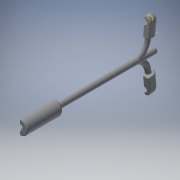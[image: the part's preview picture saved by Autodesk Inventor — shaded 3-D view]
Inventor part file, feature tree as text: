
AUTODESK INVENTOR PART (.ipt)
format: ipt  version: 2018 (Build 220112000, 112)  size: 584,704 bytes
history: native  units: mm
features: sketch x11, extrude x9, fillet x6, plane x3, projected_geometry x3, revolve x1, sweep x1, mirror x1
ambient origin geometry x8: Origin, YZ Plane, XZ Plane, XY Plane, X Axis, Y Axis, Z Axis, Center Point
bodies: Solid1 (feature_tree)
feature tree (35):
  revolve  "Revolution1"  [1 undecoded]
  fillet  "Fillet1"  Radius=8.0mm
  fillet  "Fillet2"  Radius=40.0mm
  fillet  "Fillet3"  [1 undecoded]
  plane  "Work Plane1"
  sweep  "Sweep1"
  extrude  "Extrusion2"  Depth=1.0mm
  fillet  "Fillet4"  Radius=1.5mm
  fillet  "Fillet5"  Radius=1.0mm
  extrude  "Extrusion3"  Depth=1.0mm
  extrude  "Extrusion4"  Depth=6.601018mm
  extrude  "Extrusion5"  Depth=1.0mm
  extrude  "Extrusion6"  [1 undecoded]
  extrude  "Extrusion7"  Depth=18.0mm
  plane  "Work Plane3"
  extrude  "Extrusion8"  TaperAngle=0.0deg  [1 undecoded]
  extrude  "Extrusion9"  Depth=5.0mm
  plane  "Work Plane4"
  extrude  "Extrusion10"  Depth=6.0mm
  fillet  "Fillet6"  Radius=20.0mm
  mirror  "Mirror2"
  sketch  "Sketch6"  dims[d0=150.0mm d1=3.5mm d3=8.0mm d4=40.0mm d5=90.0deg]
  sketch  "Sketch8"  dims[d20=1.5mm d21=1.5mm]
  sketch  "Sketch9"  dims[d22=1.5mm d23=1.0mm d24=1.5mm d25=1.0mm]
  projected_geometry  "Projected Loop3"
  sketch  "Sketch10"  dims[d26=1.0mm d27=1.0mm]
  projected_geometry  "Projected Loop4"
  sketch  "Sketch11"  dims[d28=1.456552mm d29=6.601018mm]
  sketch  "Sketch12"  dims[d30=2.0mm d31=1.0mm]
  sketch  "Sketch13"  dims[d32=1.0mm d33=-23.0mm]
  sketch  "Sketch14"  dims[d38=18.0mm d39=18.0mm]
  sketch  "Sketch15"  dims[d40=16.0mm d41=0.0mm d42=0.0mm]
  projected_geometry  "Projected Loop5"
  sketch  "Sketch16"  dims[d43=12.0mm d44=5.0mm]
  sketch  "Sketch17"  dims[d45=6.0mm d46=6.0mm d47=20.0mm d48=0.0mm d49=6.0mm d50=1.0mm d51=4.0mm d52=5.5mm d53=8.0mm d54=0.0mm d55=10.0mm d56=0.0mm d57=50.0mm d58=0.0mm d59=1.5mm d60=0.0mm d61=6.0mm d62=15.0mm d63=0.0mm d64=-3.0mm d65=6.5mm d66=1.1mm d67=0.0mm d68=10.0mm d69=0.0mm d70=-3.0mm d71=10.0mm d72=0.0mm d73=0.5mm]
note: 4 required parameter values undecoded (feature->parameter linkage not recoverable at this tier; creation-order binding heuristic only, values carry confidence <= 0.55)